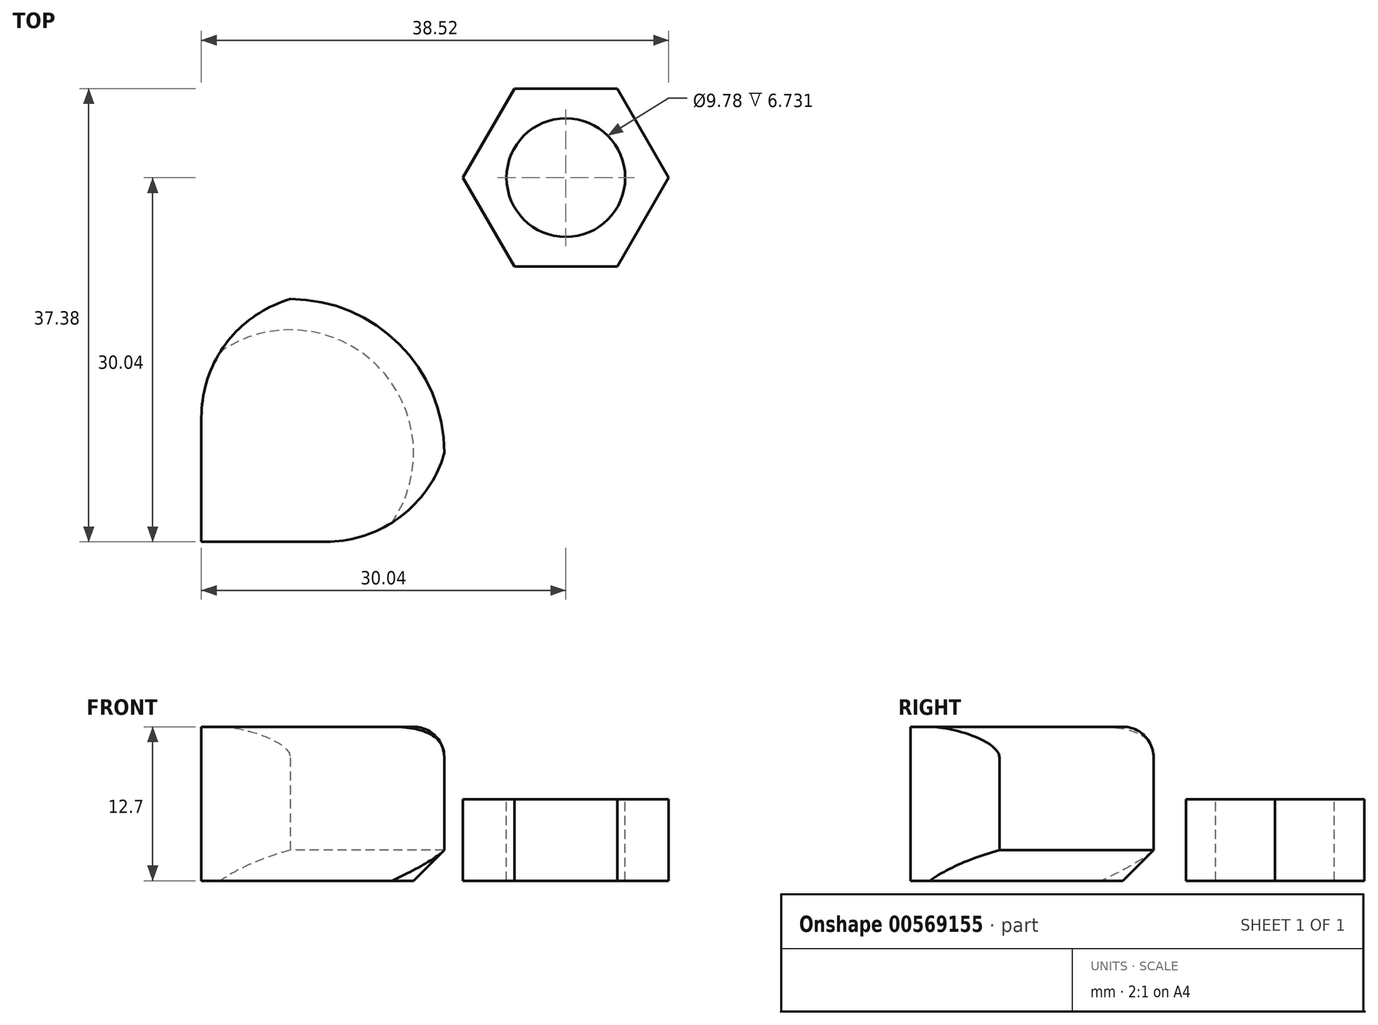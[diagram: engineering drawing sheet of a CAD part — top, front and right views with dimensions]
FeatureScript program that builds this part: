
annotation { "Feature Type Name" : "Feature", "Feature Type Description" : "" }
export const myFeature = defineFeature(function(context is Context, id is Id, definition is map)
    precondition{}
    {
        {
            var Q0;
            Q0=qCreatedBy(makeId("Top.planeOp"),FACE);
            var sketch = newSketch(context, id + "F0", { "sketchPlane" : qUnion([Q0])});
            skLineSegment(sketch, "E0", {"start": v(0, -30.04) * mm, "end": v(-30.04, -30.04) * mm});
            skLineSegment(sketch, "E1", {"start": v(-30.04, -30.04) * mm, "end": v(-30.04, 0) * mm});
            skLineSegment(sketch, "E2", {"start": v(-30.04, 0) * mm, "end": v(-30.04, 30.04) * mm});
            skLineSegment(sketch, "E3", {"start": v(-30.04, 30.04) * mm, "end": v(0, 30.04) * mm});
            skLineSegment(sketch, "E4", {"start": v(30.04, 0) * mm, "end": v(30.04, 30.04) * mm});
            skLineSegment(sketch, "E5", {"start": v(30.04, 30.04) * mm, "end": v(0, 30.04) * mm});
            skLineSegment(sketch, "E6", {"start": v(0, -30.04) * mm, "end": v(30.04, -30.04) * mm});
            skLineSegment(sketch, "E7", {"start": v(30.04, -30.04) * mm, "end": v(30.04, 0) * mm});
            skLineSegment(sketch, "E8.bottom", {"start": v(30.04, 30.04) * mm, "end": v(10.01, 30.04) * mm});
            skLineSegment(sketch, "E8.top", {"start": v(30.04, 10.01) * mm, "end": v(10.01, 10.01) * mm});
            skLineSegment(sketch, "E8.left", {"start": v(30.04, 30.04) * mm, "end": v(30.04, 10.01) * mm});
            skLineSegment(sketch, "E8.right", {"start": v(10.01, 30.04) * mm, "end": v(10.01, 10.01) * mm});
            skLineSegment(sketch, "E9.bottom", {"start": v(30.04, -30.04) * mm, "end": v(10.01, -30.04) * mm});
            skLineSegment(sketch, "E9.top", {"start": v(30.04, -10.01) * mm, "end": v(10.01, -10.01) * mm});
            skLineSegment(sketch, "E9.left", {"start": v(30.04, -30.04) * mm, "end": v(30.04, -10.01) * mm});
            skLineSegment(sketch, "E9.right", {"start": v(10.01, -30.04) * mm, "end": v(10.01, -10.01) * mm});
            skLineSegment(sketch, "E10.bottom", {"start": v(-30.04, -30.04) * mm, "end": v(-10.01, -30.04) * mm});
            skLineSegment(sketch, "E10.top", {"start": v(-30.04, -10.01) * mm, "end": v(-10.01, -10.01) * mm});
            skLineSegment(sketch, "E10.left", {"start": v(-30.04, -30.04) * mm, "end": v(-30.04, -10.01) * mm});
            skLineSegment(sketch, "E10.right", {"start": v(-10.01, -30.04) * mm, "end": v(-10.01, -10.01) * mm});
            skLineSegment(sketch, "E11.bottom", {"start": v(-30.04, 30.04) * mm, "end": v(-10.01, 30.04) * mm});
            skLineSegment(sketch, "E11.top", {"start": v(-30.04, 10.01) * mm, "end": v(-10.01, 10.01) * mm});
            skLineSegment(sketch, "E11.left", {"start": v(-30.04, 30.04) * mm, "end": v(-30.04, 10.01) * mm});
            skLineSegment(sketch, "E11.right", {"start": v(-10.01, 30.04) * mm, "end": v(-10.01, 10.01) * mm});
            skCircle(sketch, "E12.cCircle", {"center": v(0, 0) * mm, "radius": 7.34 * mm, "construction": true});
            skLineSegment(sketch, "E12.0", {"start": v(-4.24, 7.34) * mm, "end": v(4.24, 7.34) * mm});
            skLineSegment(sketch, "E12.1", {"start": v(4.24, 7.34) * mm, "end": v(8.48, 0) * mm});
            skLineSegment(sketch, "E12.2", {"start": v(8.48, 0) * mm, "end": v(4.24, -7.34) * mm});
            skLineSegment(sketch, "E12.3", {"start": v(4.24, -7.34) * mm, "end": v(-4.24, -7.34) * mm});
            skLineSegment(sketch, "E12.4", {"start": v(-4.24, -7.34) * mm, "end": v(-8.48, 0) * mm});
            skLineSegment(sketch, "E12.5", {"start": v(-8.48, 0) * mm, "end": v(-4.24, 7.34) * mm});
            skPoint(sketch, "E12.0.midPoint", {"position": v(0, 7.34) * mm});
            skSolve(sketch);
        }
        {
            var Q0;
            Q0=makeQuery(id+"F0.imprint","IMPRINT",FACE,{"disambiguationData":[TD([[makeQuery(id+"F0.imprint","IMPRINT",EDGE,{"derivedFrom":sQuery(id+"F0.wireOp",EDGE,"E0")}),-1.0]])]});
            extrude(context, id + "F1", {"entities" : qUnion([Q0]), "depth" : 12.7 * mm, "offsetDistance" : 25.4 * mm});
        }
        {
            var Q0;
            Q0=makeQuery(id+"F0.imprint","IMPRINT",FACE,{"disambiguationData":[TD([[makeQuery(id+"F0.imprint","IMPRINT",EDGE,{"derivedFrom":sQuery(id+"F0.wireOp",EDGE,"E12.0")}),-1.0]])]});
            extrude(context, id + "F2", {"entities" : qUnion([Q0]), "operationType" : NewBodyOperationType.ADD, "depth" : 6.73 * mm, "offsetDistance" : 25.4 * mm});
        }
        {
            var Q0;
            Q0=makeQuery(id+"F2.opExtrude","CAP_FACE",FACE,{"disambiguationData":[OSD([sQuery(id+"F0.wireOp",EDGE,"E12.0"),sQuery(id+"F0.wireOp",EDGE,"E12.1"),sQuery(id+"F0.wireOp",EDGE,"E12.2"),sQuery(id+"F0.wireOp",EDGE,"E12.3"),sQuery(id+"F0.wireOp",EDGE,"E12.4"),sQuery(id+"F0.wireOp",EDGE,"E12.5")])],"isStart":false});
            var sketch = newSketch(context, id + "F3", { "sketchPlane" : qUnion([Q0])});
            skCircle(sketch, "E13", {"center": v(0, 0) * mm, "radius": 4.89 * mm});
            skSolve(sketch);
        }
        {
            var Q0;
            Q0=makeQuery(id+"F3.imprint","IMPRINT",FACE,{"disambiguationData":[TD([[makeQuery(id+"F3.imprint","IMPRINT",EDGE,{"derivedFrom":sQuery(id+"F3.wireOp",EDGE,"E13")}),1.0]])]});
            extrude(context, id + "F4", {"entities" : qUnion([Q0]), "operationType" : NewBodyOperationType.REMOVE, "oppositeDirection" : true, "depth" : 25.4 * mm, "offsetDistance" : 25.4 * mm});
        }
        {
            var Q0;
            Q0=makeQuery(id+"F1.opExtrude","SWEPT_EDGE",EDGE,{"disambiguationData":[OSD([sQuery(id+"F0.wireOp",EDGE,"E9.top"),sQuery(id+"F0.wireOp",EDGE,"E9.right")])]});
            var Q1;
            Q1=makeQuery(id+"F1.opExtrude","SWEPT_EDGE",EDGE,{"disambiguationData":[OSD([sQuery(id+"F0.wireOp",EDGE,"E10.top"),sQuery(id+"F0.wireOp",EDGE,"E10.right")])]});
            var Q2;
            Q2=makeQuery(id+"F1.opExtrude","SWEPT_EDGE",EDGE,{"disambiguationData":[OSD([sQuery(id+"F0.wireOp",EDGE,"E11.top"),sQuery(id+"F0.wireOp",EDGE,"E11.right")])]});
            var Q3;
            Q3=makeQuery(id+"F1.opExtrude","SWEPT_EDGE",EDGE,{"disambiguationData":[OSD([sQuery(id+"F0.wireOp",EDGE,"E8.top"),sQuery(id+"F0.wireOp",EDGE,"E8.right")])]});
            fillet(context, id + "F5", {"entities" : qUnion([Q0, Q1, Q2, Q3]), "radius" : 12.7 * mm, "tangentPropagation" : true, "allowEdgeOverflow" : false});
        }
        {
            var Q0;
            Q0=makeQuery(id+"F1.opExtrude","SWEPT_EDGE",EDGE,{"disambiguationData":[OSD([sQuery(id+"F0.wireOp",EDGE,"E5"),sQuery(id+"F0.wireOp",EDGE,"E8.bottom"),sQuery(id+"F0.wireOp",EDGE,"E8.right")])]});
            var Q1;
            Q1=makeQuery(id+"F1.opExtrude","SWEPT_EDGE",EDGE,{"disambiguationData":[OSD([sQuery(id+"F0.wireOp",EDGE,"E3"),sQuery(id+"F0.wireOp",EDGE,"E11.bottom"),sQuery(id+"F0.wireOp",EDGE,"E11.right")])]});
            var Q2;
            Q2=makeQuery(id+"F1.opExtrude","SWEPT_EDGE",EDGE,{"disambiguationData":[OSD([sQuery(id+"F0.wireOp",EDGE,"E4"),sQuery(id+"F0.wireOp",EDGE,"E8.top"),sQuery(id+"F0.wireOp",EDGE,"E8.left")])]});
            var Q3;
            Q3=makeQuery(id+"F1.opExtrude","SWEPT_EDGE",EDGE,{"disambiguationData":[OSD([sQuery(id+"F0.wireOp",EDGE,"E7"),sQuery(id+"F0.wireOp",EDGE,"E9.top"),sQuery(id+"F0.wireOp",EDGE,"E9.left")])]});
            var Q4;
            Q4=makeQuery(id+"F1.opExtrude","SWEPT_EDGE",EDGE,{"disambiguationData":[OSD([sQuery(id+"F0.wireOp",EDGE,"E6"),sQuery(id+"F0.wireOp",EDGE,"E9.bottom"),sQuery(id+"F0.wireOp",EDGE,"E9.right")])]});
            var Q5;
            Q5=makeQuery(id+"F1.opExtrude","SWEPT_EDGE",EDGE,{"disambiguationData":[OSD([sQuery(id+"F0.wireOp",EDGE,"E0"),sQuery(id+"F0.wireOp",EDGE,"E10.bottom"),sQuery(id+"F0.wireOp",EDGE,"E10.right")])]});
            var Q6;
            Q6=makeQuery(id+"F1.opExtrude","SWEPT_EDGE",EDGE,{"disambiguationData":[OSD([sQuery(id+"F0.wireOp",EDGE,"E1"),sQuery(id+"F0.wireOp",EDGE,"E10.top"),sQuery(id+"F0.wireOp",EDGE,"E10.left")])]});
            var Q7;
            Q7=makeQuery(id+"F1.opExtrude","SWEPT_EDGE",EDGE,{"disambiguationData":[OSD([sQuery(id+"F0.wireOp",EDGE,"E2"),sQuery(id+"F0.wireOp",EDGE,"E11.top"),sQuery(id+"F0.wireOp",EDGE,"E11.left")])]});
            fillet(context, id + "F6", {"entities" : qUnion([Q0, Q1, Q2, Q3, Q4, Q5, Q6, Q7]), "radius" : 10.16 * mm, "tangentPropagation" : true, "allowEdgeOverflow" : false});
        }
        {
            var Q0;
            {var subQ0=sQuery(id+"F0.wireOp",EDGE,"E9.right");var subQ1=sQuery(id+"F0.wireOp",EDGE,"E9.top");Q0=makeQuery(id+"F5.opFillet","BLEND_EDGE",EDGE,{"blendedFrom":[makeQuery(id+"F1.opExtrude","SWEPT_EDGE",EDGE,{"disambiguationData":[OSD([subQ1,subQ0])]}),makeQuery(id+"F1.opExtrude","CAP_FACE",FACE,{"disambiguationData":[OSD([sQuery(id+"F0.wireOp",EDGE,"E0"),sQuery(id+"F0.wireOp",EDGE,"E1"),sQuery(id+"F0.wireOp",EDGE,"E2"),sQuery(id+"F0.wireOp",EDGE,"E3"),sQuery(id+"F0.wireOp",EDGE,"E4"),sQuery(id+"F0.wireOp",EDGE,"E5"),sQuery(id+"F0.wireOp",EDGE,"E6"),sQuery(id+"F0.wireOp",EDGE,"E7"),sQuery(id+"F0.wireOp",EDGE,"E8.top"),sQuery(id+"F0.wireOp",EDGE,"E8.right"),subQ1,subQ0,sQuery(id+"F0.wireOp",EDGE,"E10.top"),sQuery(id+"F0.wireOp",EDGE,"E10.right"),sQuery(id+"F0.wireOp",EDGE,"E11.top"),sQuery(id+"F0.wireOp",EDGE,"E11.right"),sQuery(id+"F0.wireOp",EDGE,"E12.0"),sQuery(id+"F0.wireOp",EDGE,"E12.1"),sQuery(id+"F0.wireOp",EDGE,"E12.2"),sQuery(id+"F0.wireOp",EDGE,"E12.3"),sQuery(id+"F0.wireOp",EDGE,"E12.4"),sQuery(id+"F0.wireOp",EDGE,"E12.5")])],"isStart":false})],"blendedInto":[makeQuery(id+"F1.opExtrude","CAP_FACE",FACE,{"disambiguationData":[OSD([sQuery(id+"F0.wireOp",EDGE,"E0"),sQuery(id+"F0.wireOp",EDGE,"E1"),sQuery(id+"F0.wireOp",EDGE,"E2"),sQuery(id+"F0.wireOp",EDGE,"E3"),sQuery(id+"F0.wireOp",EDGE,"E4"),sQuery(id+"F0.wireOp",EDGE,"E5"),sQuery(id+"F0.wireOp",EDGE,"E6"),sQuery(id+"F0.wireOp",EDGE,"E7"),sQuery(id+"F0.wireOp",EDGE,"E8.top"),sQuery(id+"F0.wireOp",EDGE,"E8.right"),subQ1,subQ0,sQuery(id+"F0.wireOp",EDGE,"E10.top"),sQuery(id+"F0.wireOp",EDGE,"E10.right"),sQuery(id+"F0.wireOp",EDGE,"E11.top"),sQuery(id+"F0.wireOp",EDGE,"E11.right"),sQuery(id+"F0.wireOp",EDGE,"E12.0"),sQuery(id+"F0.wireOp",EDGE,"E12.1"),sQuery(id+"F0.wireOp",EDGE,"E12.2"),sQuery(id+"F0.wireOp",EDGE,"E12.3"),sQuery(id+"F0.wireOp",EDGE,"E12.4"),sQuery(id+"F0.wireOp",EDGE,"E12.5")])],"isStart":false})]});}
            var Q1;
            {var subQ0=sQuery(id+"F0.wireOp",EDGE,"E8.right");var subQ1=sQuery(id+"F0.wireOp",EDGE,"E8.top");Q1=makeQuery(id+"F5.opFillet","BLEND_EDGE",EDGE,{"blendedFrom":[makeQuery(id+"F1.opExtrude","SWEPT_EDGE",EDGE,{"disambiguationData":[OSD([subQ1,subQ0])]}),makeQuery(id+"F1.opExtrude","CAP_FACE",FACE,{"disambiguationData":[OSD([sQuery(id+"F0.wireOp",EDGE,"E0"),sQuery(id+"F0.wireOp",EDGE,"E1"),sQuery(id+"F0.wireOp",EDGE,"E2"),sQuery(id+"F0.wireOp",EDGE,"E3"),sQuery(id+"F0.wireOp",EDGE,"E4"),sQuery(id+"F0.wireOp",EDGE,"E5"),sQuery(id+"F0.wireOp",EDGE,"E6"),sQuery(id+"F0.wireOp",EDGE,"E7"),subQ1,subQ0,sQuery(id+"F0.wireOp",EDGE,"E9.top"),sQuery(id+"F0.wireOp",EDGE,"E9.right"),sQuery(id+"F0.wireOp",EDGE,"E10.top"),sQuery(id+"F0.wireOp",EDGE,"E10.right"),sQuery(id+"F0.wireOp",EDGE,"E11.top"),sQuery(id+"F0.wireOp",EDGE,"E11.right"),sQuery(id+"F0.wireOp",EDGE,"E12.0"),sQuery(id+"F0.wireOp",EDGE,"E12.1"),sQuery(id+"F0.wireOp",EDGE,"E12.2"),sQuery(id+"F0.wireOp",EDGE,"E12.3"),sQuery(id+"F0.wireOp",EDGE,"E12.4"),sQuery(id+"F0.wireOp",EDGE,"E12.5")])],"isStart":false})],"blendedInto":[makeQuery(id+"F1.opExtrude","CAP_FACE",FACE,{"disambiguationData":[OSD([sQuery(id+"F0.wireOp",EDGE,"E0"),sQuery(id+"F0.wireOp",EDGE,"E1"),sQuery(id+"F0.wireOp",EDGE,"E2"),sQuery(id+"F0.wireOp",EDGE,"E3"),sQuery(id+"F0.wireOp",EDGE,"E4"),sQuery(id+"F0.wireOp",EDGE,"E5"),sQuery(id+"F0.wireOp",EDGE,"E6"),sQuery(id+"F0.wireOp",EDGE,"E7"),subQ1,subQ0,sQuery(id+"F0.wireOp",EDGE,"E9.top"),sQuery(id+"F0.wireOp",EDGE,"E9.right"),sQuery(id+"F0.wireOp",EDGE,"E10.top"),sQuery(id+"F0.wireOp",EDGE,"E10.right"),sQuery(id+"F0.wireOp",EDGE,"E11.top"),sQuery(id+"F0.wireOp",EDGE,"E11.right"),sQuery(id+"F0.wireOp",EDGE,"E12.0"),sQuery(id+"F0.wireOp",EDGE,"E12.1"),sQuery(id+"F0.wireOp",EDGE,"E12.2"),sQuery(id+"F0.wireOp",EDGE,"E12.3"),sQuery(id+"F0.wireOp",EDGE,"E12.4"),sQuery(id+"F0.wireOp",EDGE,"E12.5")])],"isStart":false})]});}
            var Q2;
            {var subQ0=sQuery(id+"F0.wireOp",EDGE,"E11.right");var subQ1=sQuery(id+"F0.wireOp",EDGE,"E11.top");Q2=makeQuery(id+"F5.opFillet","BLEND_EDGE",EDGE,{"blendedFrom":[makeQuery(id+"F1.opExtrude","SWEPT_EDGE",EDGE,{"disambiguationData":[OSD([subQ1,subQ0])]}),makeQuery(id+"F1.opExtrude","CAP_FACE",FACE,{"disambiguationData":[OSD([sQuery(id+"F0.wireOp",EDGE,"E0"),sQuery(id+"F0.wireOp",EDGE,"E1"),sQuery(id+"F0.wireOp",EDGE,"E2"),sQuery(id+"F0.wireOp",EDGE,"E3"),sQuery(id+"F0.wireOp",EDGE,"E4"),sQuery(id+"F0.wireOp",EDGE,"E5"),sQuery(id+"F0.wireOp",EDGE,"E6"),sQuery(id+"F0.wireOp",EDGE,"E7"),sQuery(id+"F0.wireOp",EDGE,"E8.top"),sQuery(id+"F0.wireOp",EDGE,"E8.right"),sQuery(id+"F0.wireOp",EDGE,"E9.top"),sQuery(id+"F0.wireOp",EDGE,"E9.right"),sQuery(id+"F0.wireOp",EDGE,"E10.top"),sQuery(id+"F0.wireOp",EDGE,"E10.right"),subQ1,subQ0,sQuery(id+"F0.wireOp",EDGE,"E12.0"),sQuery(id+"F0.wireOp",EDGE,"E12.1"),sQuery(id+"F0.wireOp",EDGE,"E12.2"),sQuery(id+"F0.wireOp",EDGE,"E12.3"),sQuery(id+"F0.wireOp",EDGE,"E12.4"),sQuery(id+"F0.wireOp",EDGE,"E12.5")])],"isStart":false})],"blendedInto":[makeQuery(id+"F1.opExtrude","CAP_FACE",FACE,{"disambiguationData":[OSD([sQuery(id+"F0.wireOp",EDGE,"E0"),sQuery(id+"F0.wireOp",EDGE,"E1"),sQuery(id+"F0.wireOp",EDGE,"E2"),sQuery(id+"F0.wireOp",EDGE,"E3"),sQuery(id+"F0.wireOp",EDGE,"E4"),sQuery(id+"F0.wireOp",EDGE,"E5"),sQuery(id+"F0.wireOp",EDGE,"E6"),sQuery(id+"F0.wireOp",EDGE,"E7"),sQuery(id+"F0.wireOp",EDGE,"E8.top"),sQuery(id+"F0.wireOp",EDGE,"E8.right"),sQuery(id+"F0.wireOp",EDGE,"E9.top"),sQuery(id+"F0.wireOp",EDGE,"E9.right"),sQuery(id+"F0.wireOp",EDGE,"E10.top"),sQuery(id+"F0.wireOp",EDGE,"E10.right"),subQ1,subQ0,sQuery(id+"F0.wireOp",EDGE,"E12.0"),sQuery(id+"F0.wireOp",EDGE,"E12.1"),sQuery(id+"F0.wireOp",EDGE,"E12.2"),sQuery(id+"F0.wireOp",EDGE,"E12.3"),sQuery(id+"F0.wireOp",EDGE,"E12.4"),sQuery(id+"F0.wireOp",EDGE,"E12.5")])],"isStart":false})]});}
            var Q3;
            {var subQ0=sQuery(id+"F0.wireOp",EDGE,"E10.right");var subQ1=sQuery(id+"F0.wireOp",EDGE,"E10.top");Q3=makeQuery(id+"F5.opFillet","BLEND_EDGE",EDGE,{"blendedFrom":[makeQuery(id+"F1.opExtrude","SWEPT_EDGE",EDGE,{"disambiguationData":[OSD([subQ1,subQ0])]}),makeQuery(id+"F1.opExtrude","CAP_FACE",FACE,{"disambiguationData":[OSD([sQuery(id+"F0.wireOp",EDGE,"E0"),sQuery(id+"F0.wireOp",EDGE,"E1"),sQuery(id+"F0.wireOp",EDGE,"E2"),sQuery(id+"F0.wireOp",EDGE,"E3"),sQuery(id+"F0.wireOp",EDGE,"E4"),sQuery(id+"F0.wireOp",EDGE,"E5"),sQuery(id+"F0.wireOp",EDGE,"E6"),sQuery(id+"F0.wireOp",EDGE,"E7"),sQuery(id+"F0.wireOp",EDGE,"E8.top"),sQuery(id+"F0.wireOp",EDGE,"E8.right"),sQuery(id+"F0.wireOp",EDGE,"E9.top"),sQuery(id+"F0.wireOp",EDGE,"E9.right"),subQ1,subQ0,sQuery(id+"F0.wireOp",EDGE,"E11.top"),sQuery(id+"F0.wireOp",EDGE,"E11.right"),sQuery(id+"F0.wireOp",EDGE,"E12.0"),sQuery(id+"F0.wireOp",EDGE,"E12.1"),sQuery(id+"F0.wireOp",EDGE,"E12.2"),sQuery(id+"F0.wireOp",EDGE,"E12.3"),sQuery(id+"F0.wireOp",EDGE,"E12.4"),sQuery(id+"F0.wireOp",EDGE,"E12.5")])],"isStart":false})],"blendedInto":[makeQuery(id+"F1.opExtrude","CAP_FACE",FACE,{"disambiguationData":[OSD([sQuery(id+"F0.wireOp",EDGE,"E0"),sQuery(id+"F0.wireOp",EDGE,"E1"),sQuery(id+"F0.wireOp",EDGE,"E2"),sQuery(id+"F0.wireOp",EDGE,"E3"),sQuery(id+"F0.wireOp",EDGE,"E4"),sQuery(id+"F0.wireOp",EDGE,"E5"),sQuery(id+"F0.wireOp",EDGE,"E6"),sQuery(id+"F0.wireOp",EDGE,"E7"),sQuery(id+"F0.wireOp",EDGE,"E8.top"),sQuery(id+"F0.wireOp",EDGE,"E8.right"),sQuery(id+"F0.wireOp",EDGE,"E9.top"),sQuery(id+"F0.wireOp",EDGE,"E9.right"),subQ1,subQ0,sQuery(id+"F0.wireOp",EDGE,"E11.top"),sQuery(id+"F0.wireOp",EDGE,"E11.right"),sQuery(id+"F0.wireOp",EDGE,"E12.0"),sQuery(id+"F0.wireOp",EDGE,"E12.1"),sQuery(id+"F0.wireOp",EDGE,"E12.2"),sQuery(id+"F0.wireOp",EDGE,"E12.3"),sQuery(id+"F0.wireOp",EDGE,"E12.4"),sQuery(id+"F0.wireOp",EDGE,"E12.5")])],"isStart":false})]});}
            fillet(context, id + "F7", {"entities" : qUnion([Q0, Q1, Q2, Q3]), "radius" : 2.54 * mm, "tangentPropagation" : true, "allowEdgeOverflow" : false});
        }
        {
            var Q0;
            {var subQ0=sQuery(id+"F0.wireOp",EDGE,"E12.5");var subQ1=sQuery(id+"F0.wireOp",EDGE,"E12.4");var subQ2=sQuery(id+"F0.wireOp",EDGE,"E12.3");var subQ3=sQuery(id+"F0.wireOp",EDGE,"E12.2");var subQ4=sQuery(id+"F0.wireOp",EDGE,"E12.1");var subQ5=sQuery(id+"F0.wireOp",EDGE,"E12.0");var subQ6=sQuery(id+"F0.wireOp",EDGE,"E9.right");var subQ7=sQuery(id+"F0.wireOp",EDGE,"E9.top");Q0=makeQuery(id+"F5.opFillet","BLEND_EDGE",EDGE,{"blendedFrom":[makeQuery(id+"F1.opExtrude","SWEPT_EDGE",EDGE,{"disambiguationData":[OSD([subQ7,subQ6])]}),makeQuery(id+"F2.boolean.opBoolean","MERGE",FACE,{"derivedFrom":[makeQuery(id+"F1.opExtrude","CAP_FACE",FACE,{"disambiguationData":[OSD([sQuery(id+"F0.wireOp",EDGE,"E0"),sQuery(id+"F0.wireOp",EDGE,"E1"),sQuery(id+"F0.wireOp",EDGE,"E2"),sQuery(id+"F0.wireOp",EDGE,"E3"),sQuery(id+"F0.wireOp",EDGE,"E4"),sQuery(id+"F0.wireOp",EDGE,"E5"),sQuery(id+"F0.wireOp",EDGE,"E6"),sQuery(id+"F0.wireOp",EDGE,"E7"),sQuery(id+"F0.wireOp",EDGE,"E8.top"),sQuery(id+"F0.wireOp",EDGE,"E8.right"),subQ7,subQ6,sQuery(id+"F0.wireOp",EDGE,"E10.top"),sQuery(id+"F0.wireOp",EDGE,"E10.right"),sQuery(id+"F0.wireOp",EDGE,"E11.top"),sQuery(id+"F0.wireOp",EDGE,"E11.right"),subQ5,subQ4,subQ3,subQ2,subQ1,subQ0])],"isStart":true}),makeQuery(id+"F2.opExtrude","CAP_FACE",FACE,{"disambiguationData":[OSD([subQ5,subQ4,subQ3,subQ2,subQ1,subQ0])],"isStart":true})]})],"blendedInto":[makeQuery(id+"F2.boolean.opBoolean","MERGE",FACE,{"derivedFrom":[makeQuery(id+"F1.opExtrude","CAP_FACE",FACE,{"disambiguationData":[OSD([sQuery(id+"F0.wireOp",EDGE,"E0"),sQuery(id+"F0.wireOp",EDGE,"E1"),sQuery(id+"F0.wireOp",EDGE,"E2"),sQuery(id+"F0.wireOp",EDGE,"E3"),sQuery(id+"F0.wireOp",EDGE,"E4"),sQuery(id+"F0.wireOp",EDGE,"E5"),sQuery(id+"F0.wireOp",EDGE,"E6"),sQuery(id+"F0.wireOp",EDGE,"E7"),sQuery(id+"F0.wireOp",EDGE,"E8.top"),sQuery(id+"F0.wireOp",EDGE,"E8.right"),subQ7,subQ6,sQuery(id+"F0.wireOp",EDGE,"E10.top"),sQuery(id+"F0.wireOp",EDGE,"E10.right"),sQuery(id+"F0.wireOp",EDGE,"E11.top"),sQuery(id+"F0.wireOp",EDGE,"E11.right"),subQ5,subQ4,subQ3,subQ2,subQ1,subQ0])],"isStart":true}),makeQuery(id+"F2.opExtrude","CAP_FACE",FACE,{"disambiguationData":[OSD([subQ5,subQ4,subQ3,subQ2,subQ1,subQ0])],"isStart":true})]})]});}
            var Q1;
            {var subQ0=sQuery(id+"F0.wireOp",EDGE,"E12.5");var subQ1=sQuery(id+"F0.wireOp",EDGE,"E12.4");var subQ2=sQuery(id+"F0.wireOp",EDGE,"E12.3");var subQ3=sQuery(id+"F0.wireOp",EDGE,"E12.2");var subQ4=sQuery(id+"F0.wireOp",EDGE,"E12.1");var subQ5=sQuery(id+"F0.wireOp",EDGE,"E12.0");var subQ6=sQuery(id+"F0.wireOp",EDGE,"E10.right");var subQ7=sQuery(id+"F0.wireOp",EDGE,"E10.top");Q1=makeQuery(id+"F5.opFillet","BLEND_EDGE",EDGE,{"blendedFrom":[makeQuery(id+"F1.opExtrude","SWEPT_EDGE",EDGE,{"disambiguationData":[OSD([subQ7,subQ6])]}),makeQuery(id+"F2.boolean.opBoolean","MERGE",FACE,{"derivedFrom":[makeQuery(id+"F1.opExtrude","CAP_FACE",FACE,{"disambiguationData":[OSD([sQuery(id+"F0.wireOp",EDGE,"E0"),sQuery(id+"F0.wireOp",EDGE,"E1"),sQuery(id+"F0.wireOp",EDGE,"E2"),sQuery(id+"F0.wireOp",EDGE,"E3"),sQuery(id+"F0.wireOp",EDGE,"E4"),sQuery(id+"F0.wireOp",EDGE,"E5"),sQuery(id+"F0.wireOp",EDGE,"E6"),sQuery(id+"F0.wireOp",EDGE,"E7"),sQuery(id+"F0.wireOp",EDGE,"E8.top"),sQuery(id+"F0.wireOp",EDGE,"E8.right"),sQuery(id+"F0.wireOp",EDGE,"E9.top"),sQuery(id+"F0.wireOp",EDGE,"E9.right"),subQ7,subQ6,sQuery(id+"F0.wireOp",EDGE,"E11.top"),sQuery(id+"F0.wireOp",EDGE,"E11.right"),subQ5,subQ4,subQ3,subQ2,subQ1,subQ0])],"isStart":true}),makeQuery(id+"F2.opExtrude","CAP_FACE",FACE,{"disambiguationData":[OSD([subQ5,subQ4,subQ3,subQ2,subQ1,subQ0])],"isStart":true})]})],"blendedInto":[makeQuery(id+"F2.boolean.opBoolean","MERGE",FACE,{"derivedFrom":[makeQuery(id+"F1.opExtrude","CAP_FACE",FACE,{"disambiguationData":[OSD([sQuery(id+"F0.wireOp",EDGE,"E0"),sQuery(id+"F0.wireOp",EDGE,"E1"),sQuery(id+"F0.wireOp",EDGE,"E2"),sQuery(id+"F0.wireOp",EDGE,"E3"),sQuery(id+"F0.wireOp",EDGE,"E4"),sQuery(id+"F0.wireOp",EDGE,"E5"),sQuery(id+"F0.wireOp",EDGE,"E6"),sQuery(id+"F0.wireOp",EDGE,"E7"),sQuery(id+"F0.wireOp",EDGE,"E8.top"),sQuery(id+"F0.wireOp",EDGE,"E8.right"),sQuery(id+"F0.wireOp",EDGE,"E9.top"),sQuery(id+"F0.wireOp",EDGE,"E9.right"),subQ7,subQ6,sQuery(id+"F0.wireOp",EDGE,"E11.top"),sQuery(id+"F0.wireOp",EDGE,"E11.right"),subQ5,subQ4,subQ3,subQ2,subQ1,subQ0])],"isStart":true}),makeQuery(id+"F2.opExtrude","CAP_FACE",FACE,{"disambiguationData":[OSD([subQ5,subQ4,subQ3,subQ2,subQ1,subQ0])],"isStart":true})]})]});}
            var Q2;
            {var subQ0=sQuery(id+"F0.wireOp",EDGE,"E12.5");var subQ1=sQuery(id+"F0.wireOp",EDGE,"E12.4");var subQ2=sQuery(id+"F0.wireOp",EDGE,"E12.3");var subQ3=sQuery(id+"F0.wireOp",EDGE,"E12.2");var subQ4=sQuery(id+"F0.wireOp",EDGE,"E12.1");var subQ5=sQuery(id+"F0.wireOp",EDGE,"E12.0");var subQ6=sQuery(id+"F0.wireOp",EDGE,"E11.right");var subQ7=sQuery(id+"F0.wireOp",EDGE,"E11.top");Q2=makeQuery(id+"F5.opFillet","BLEND_EDGE",EDGE,{"blendedFrom":[makeQuery(id+"F1.opExtrude","SWEPT_EDGE",EDGE,{"disambiguationData":[OSD([subQ7,subQ6])]}),makeQuery(id+"F2.boolean.opBoolean","MERGE",FACE,{"derivedFrom":[makeQuery(id+"F1.opExtrude","CAP_FACE",FACE,{"disambiguationData":[OSD([sQuery(id+"F0.wireOp",EDGE,"E0"),sQuery(id+"F0.wireOp",EDGE,"E1"),sQuery(id+"F0.wireOp",EDGE,"E2"),sQuery(id+"F0.wireOp",EDGE,"E3"),sQuery(id+"F0.wireOp",EDGE,"E4"),sQuery(id+"F0.wireOp",EDGE,"E5"),sQuery(id+"F0.wireOp",EDGE,"E6"),sQuery(id+"F0.wireOp",EDGE,"E7"),sQuery(id+"F0.wireOp",EDGE,"E8.top"),sQuery(id+"F0.wireOp",EDGE,"E8.right"),sQuery(id+"F0.wireOp",EDGE,"E9.top"),sQuery(id+"F0.wireOp",EDGE,"E9.right"),sQuery(id+"F0.wireOp",EDGE,"E10.top"),sQuery(id+"F0.wireOp",EDGE,"E10.right"),subQ7,subQ6,subQ5,subQ4,subQ3,subQ2,subQ1,subQ0])],"isStart":true}),makeQuery(id+"F2.opExtrude","CAP_FACE",FACE,{"disambiguationData":[OSD([subQ5,subQ4,subQ3,subQ2,subQ1,subQ0])],"isStart":true})]})],"blendedInto":[makeQuery(id+"F2.boolean.opBoolean","MERGE",FACE,{"derivedFrom":[makeQuery(id+"F1.opExtrude","CAP_FACE",FACE,{"disambiguationData":[OSD([sQuery(id+"F0.wireOp",EDGE,"E0"),sQuery(id+"F0.wireOp",EDGE,"E1"),sQuery(id+"F0.wireOp",EDGE,"E2"),sQuery(id+"F0.wireOp",EDGE,"E3"),sQuery(id+"F0.wireOp",EDGE,"E4"),sQuery(id+"F0.wireOp",EDGE,"E5"),sQuery(id+"F0.wireOp",EDGE,"E6"),sQuery(id+"F0.wireOp",EDGE,"E7"),sQuery(id+"F0.wireOp",EDGE,"E8.top"),sQuery(id+"F0.wireOp",EDGE,"E8.right"),sQuery(id+"F0.wireOp",EDGE,"E9.top"),sQuery(id+"F0.wireOp",EDGE,"E9.right"),sQuery(id+"F0.wireOp",EDGE,"E10.top"),sQuery(id+"F0.wireOp",EDGE,"E10.right"),subQ7,subQ6,subQ5,subQ4,subQ3,subQ2,subQ1,subQ0])],"isStart":true}),makeQuery(id+"F2.opExtrude","CAP_FACE",FACE,{"disambiguationData":[OSD([subQ5,subQ4,subQ3,subQ2,subQ1,subQ0])],"isStart":true})]})]});}
            var Q3;
            {var subQ0=sQuery(id+"F0.wireOp",EDGE,"E12.5");var subQ1=sQuery(id+"F0.wireOp",EDGE,"E12.4");var subQ2=sQuery(id+"F0.wireOp",EDGE,"E12.3");var subQ3=sQuery(id+"F0.wireOp",EDGE,"E12.2");var subQ4=sQuery(id+"F0.wireOp",EDGE,"E12.1");var subQ5=sQuery(id+"F0.wireOp",EDGE,"E12.0");var subQ6=sQuery(id+"F0.wireOp",EDGE,"E8.right");var subQ7=sQuery(id+"F0.wireOp",EDGE,"E8.top");Q3=makeQuery(id+"F5.opFillet","BLEND_EDGE",EDGE,{"blendedFrom":[makeQuery(id+"F1.opExtrude","SWEPT_EDGE",EDGE,{"disambiguationData":[OSD([subQ7,subQ6])]}),makeQuery(id+"F2.boolean.opBoolean","MERGE",FACE,{"derivedFrom":[makeQuery(id+"F1.opExtrude","CAP_FACE",FACE,{"disambiguationData":[OSD([sQuery(id+"F0.wireOp",EDGE,"E0"),sQuery(id+"F0.wireOp",EDGE,"E1"),sQuery(id+"F0.wireOp",EDGE,"E2"),sQuery(id+"F0.wireOp",EDGE,"E3"),sQuery(id+"F0.wireOp",EDGE,"E4"),sQuery(id+"F0.wireOp",EDGE,"E5"),sQuery(id+"F0.wireOp",EDGE,"E6"),sQuery(id+"F0.wireOp",EDGE,"E7"),subQ7,subQ6,sQuery(id+"F0.wireOp",EDGE,"E9.top"),sQuery(id+"F0.wireOp",EDGE,"E9.right"),sQuery(id+"F0.wireOp",EDGE,"E10.top"),sQuery(id+"F0.wireOp",EDGE,"E10.right"),sQuery(id+"F0.wireOp",EDGE,"E11.top"),sQuery(id+"F0.wireOp",EDGE,"E11.right"),subQ5,subQ4,subQ3,subQ2,subQ1,subQ0])],"isStart":true}),makeQuery(id+"F2.opExtrude","CAP_FACE",FACE,{"disambiguationData":[OSD([subQ5,subQ4,subQ3,subQ2,subQ1,subQ0])],"isStart":true})]})],"blendedInto":[makeQuery(id+"F2.boolean.opBoolean","MERGE",FACE,{"derivedFrom":[makeQuery(id+"F1.opExtrude","CAP_FACE",FACE,{"disambiguationData":[OSD([sQuery(id+"F0.wireOp",EDGE,"E0"),sQuery(id+"F0.wireOp",EDGE,"E1"),sQuery(id+"F0.wireOp",EDGE,"E2"),sQuery(id+"F0.wireOp",EDGE,"E3"),sQuery(id+"F0.wireOp",EDGE,"E4"),sQuery(id+"F0.wireOp",EDGE,"E5"),sQuery(id+"F0.wireOp",EDGE,"E6"),sQuery(id+"F0.wireOp",EDGE,"E7"),subQ7,subQ6,sQuery(id+"F0.wireOp",EDGE,"E9.top"),sQuery(id+"F0.wireOp",EDGE,"E9.right"),sQuery(id+"F0.wireOp",EDGE,"E10.top"),sQuery(id+"F0.wireOp",EDGE,"E10.right"),sQuery(id+"F0.wireOp",EDGE,"E11.top"),sQuery(id+"F0.wireOp",EDGE,"E11.right"),subQ5,subQ4,subQ3,subQ2,subQ1,subQ0])],"isStart":true}),makeQuery(id+"F2.opExtrude","CAP_FACE",FACE,{"disambiguationData":[OSD([subQ5,subQ4,subQ3,subQ2,subQ1,subQ0])],"isStart":true})]})]});}
            chamfer(context, id + "F8", {"entities" : qUnion([Q0, Q1, Q2, Q3]), "width" : 2.54 * mm, "tangentPropagation" : true});
        }
    });
